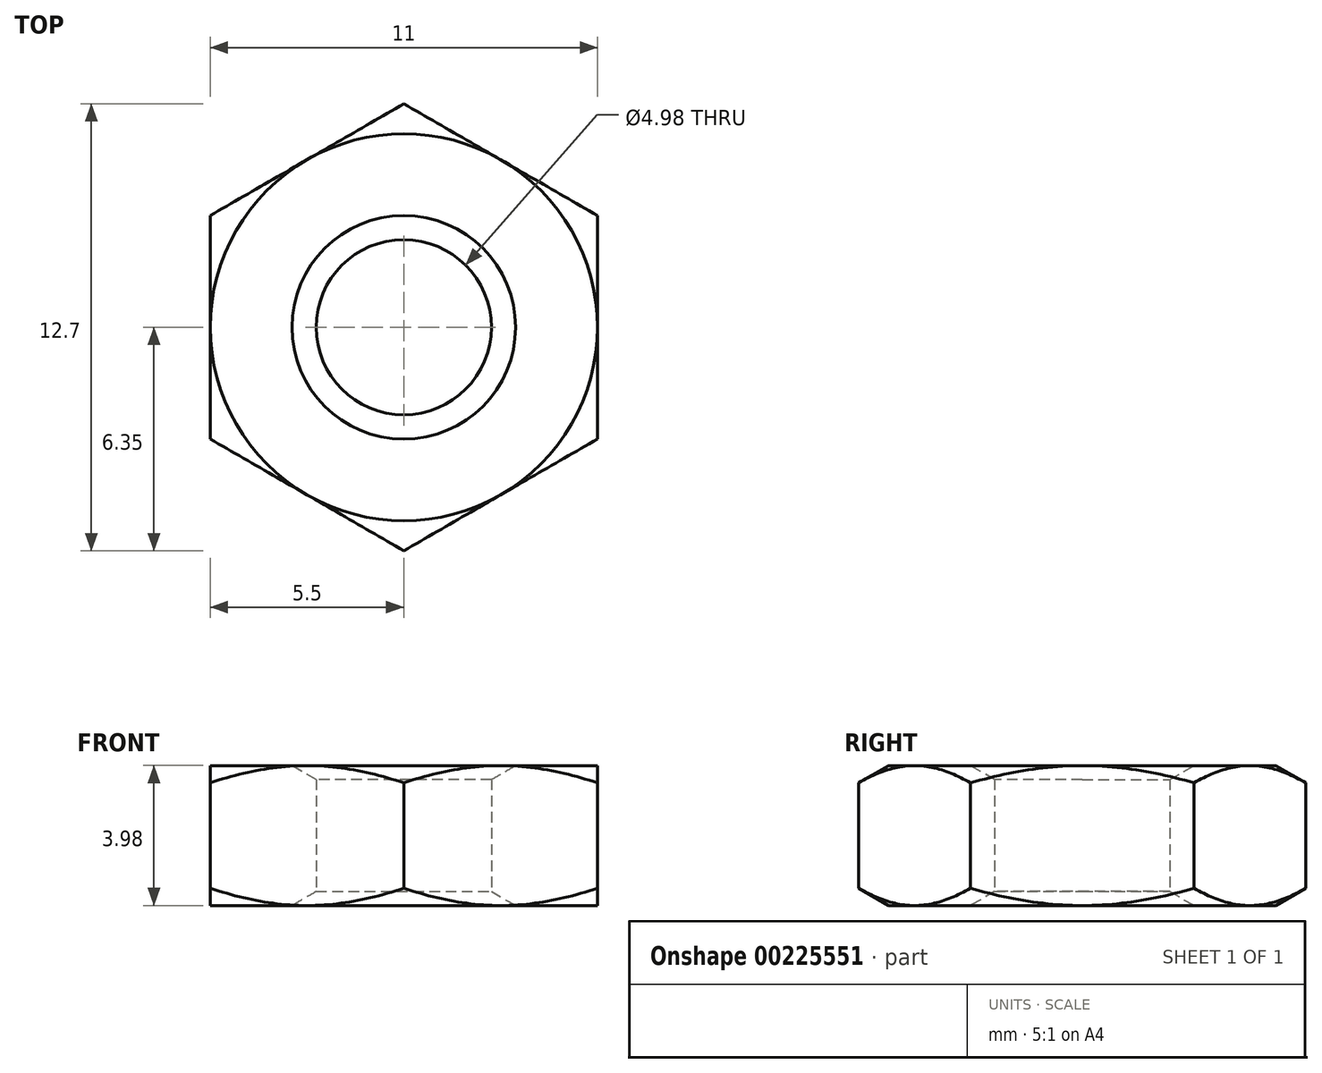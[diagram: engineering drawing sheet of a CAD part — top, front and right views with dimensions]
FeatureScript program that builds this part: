
annotation { "Feature Type Name" : "Feature", "Feature Type Description" : "" }
export const myFeature = defineFeature(function(context is Context, id is Id, definition is map)
    precondition{}
    {
        {
            var Q0;
            Q0=qCreatedBy(makeId("Top.planeOp"),FACE);
            var sketch = newSketch(context, id + "F0", { "sketchPlane" : qUnion([Q0])});
            skCircle(sketch, "E0", {"center": v(0, 0) * mm, "radius": 3.18 * mm});
            skCircle(sketch, "E1.cCircle", {"center": v(0, 0) * mm, "radius": 5.5 * mm, "construction": true});
            skLineSegment(sketch, "E1.0", {"start": v(5.5, 3.17) * mm, "end": v(5.5, -3.17) * mm});
            skLineSegment(sketch, "E1.1", {"start": v(5.5, -3.17) * mm, "end": v(0, -6.35) * mm});
            skLineSegment(sketch, "E1.2", {"start": v(0, -6.35) * mm, "end": v(-5.5, -3.17) * mm});
            skLineSegment(sketch, "E1.3", {"start": v(-5.5, -3.17) * mm, "end": v(-5.5, 3.17) * mm});
            skLineSegment(sketch, "E1.4", {"start": v(-5.5, 3.17) * mm, "end": v(0, 6.35) * mm});
            skLineSegment(sketch, "E1.5", {"start": v(0, 6.35) * mm, "end": v(5.5, 3.17) * mm});
            skPoint(sketch, "E1.0.midPoint", {"position": v(5.5, 0) * mm});
            skCircle(sketch, "E2", {"center": v(0, 0) * mm, "radius": 2.49 * mm});
            skSolve(sketch);
        }
        {
            var Q0;
            Q0 = qSketchRegion(id + "F0", true);
            var Q1;
            Q1=makeQuery(id+"F0.imprint","IMPRINT",FACE,{"disambiguationData":[TD([[makeQuery(id+"F0.imprint","IMPRINT",EDGE,{"derivedFrom":sQuery(id+"F0.wireOp",EDGE,"E0")}),1.0]])]});
            extrude(context, id + "F1", {"entities" : qUnion([Q0, Q1]), "depth" : 3.98 * mm});
        }
        {
            var Q0;
            Q0=qCreatedBy(makeId("Front.planeOp"),FACE);
            var sketch = newSketch(context, id + "F2", { "sketchPlane" : qUnion([Q0])});
            skLineSegment(sketch, "E3.0", {"start": v(5.5, 3.98) * mm, "end": v(0, 3.98) * mm});
            skLineSegment(sketch, "E4.0", {"start": v(5.5, 3.98) * mm, "end": v(5.5, 0) * mm});
            skLineSegment(sketch, "E5.0", {"start": v(5.5, 0) * mm, "end": v(0, 0) * mm});
            skLineSegment(sketch, "E6", {"start": v(0, 3.98) * mm, "end": v(0, 0) * mm});
            skLineSegment(sketch, "E7", {"start": v(0, 2.14) * mm, "end": v(3.18, 3.98) * mm});
            skLineSegment(sketch, "E8", {"start": v(5.5, 3.98) * mm, "end": v(8.04, 3.98) * mm});
            skLineSegment(sketch, "E9", {"start": v(8.04, 3.98) * mm, "end": v(8.04, 0) * mm});
            skLineSegment(sketch, "E10", {"start": v(8.04, 0) * mm, "end": v(5.5, 0) * mm});
            skLineSegment(sketch, "E11", {"start": v(5.5, 0) * mm, "end": v(8.04, 1.47) * mm});
            skLineSegment(sketch, "E12", {"start": v(5.5, 3.98) * mm, "end": v(8.04, 2.5) * mm});
            skLineSegment(sketch, "E13", {"start": v(0, 1.83) * mm, "end": v(3.18, 0) * mm});
            skSolve(sketch);
        }
        {
            var Q0;
            {var subQ4=sQuery(id+"F2.wireOp",EDGE,"E4.0");Q0=makeQuery(id+"F2.imprint","IMPRINT",FACE,{"disambiguationData":[TD([[makeQuery(id+"F2.imprint","IMPRINT",EDGE,{"derivedFrom":subQ4}),-1.0]])]});}
            var Q1;
            Q1=makeQuery(id+"F2.imprint","IMPRINT",FACE,{"disambiguationData":[TD([[makeQuery(id+"F2.imprint","IMPRINT",EDGE,{"derivedFrom":sQuery(id+"F2.wireOp",EDGE,"E4.0")}),1.0]])]});
            var Q2;
            Q2=sQuery(id+"F2.wireOp",EDGE,"E6");
            revolve(context, id + "F3", {"operationType" : NewBodyOperationType.INTERSECT, "entities" : qUnion([Q0, Q1]), "axis" : qUnion([Q2]), "revolveType" : RevolveType.FULL, "oppositeDirection" : true});
        }
    });
